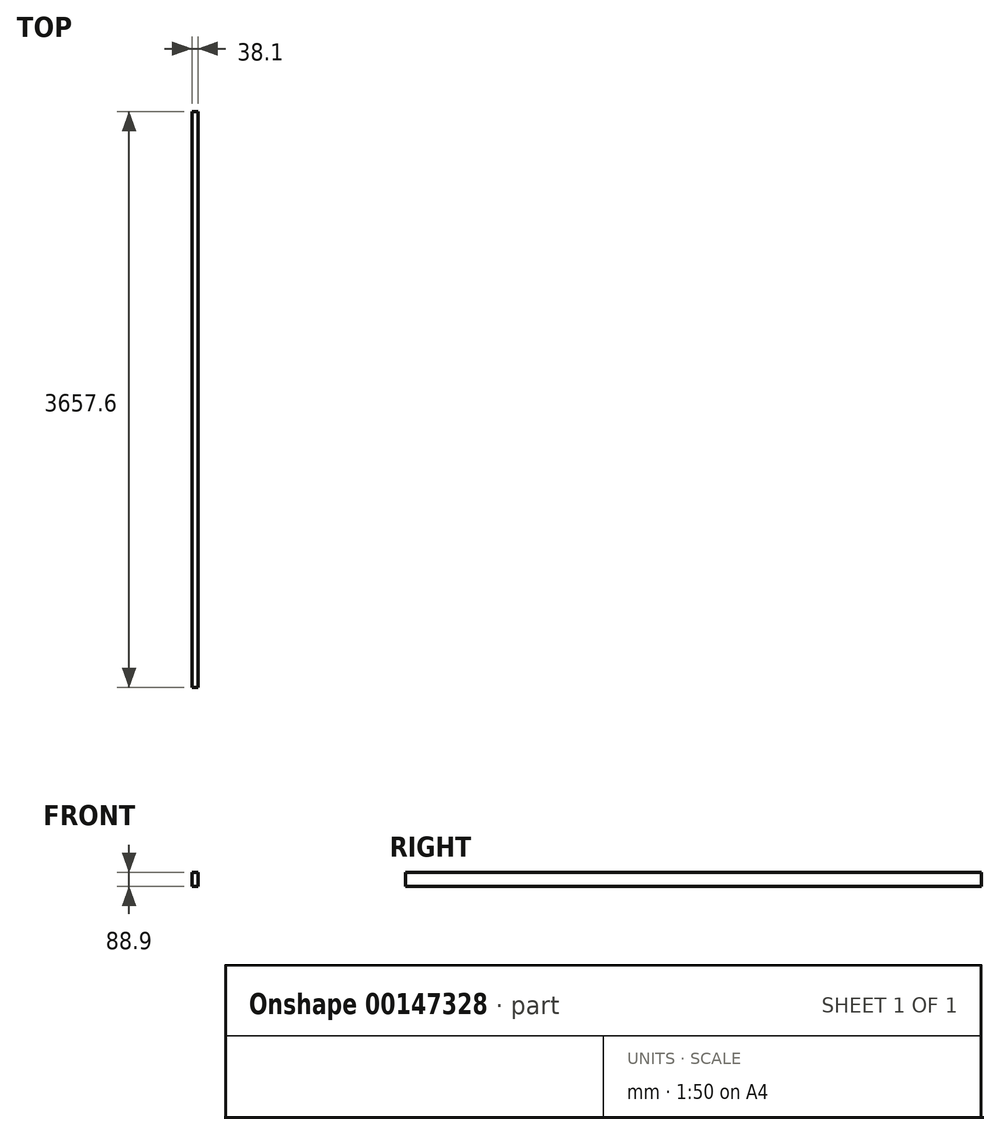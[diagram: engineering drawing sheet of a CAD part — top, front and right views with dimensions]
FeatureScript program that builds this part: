
annotation { "Feature Type Name" : "Feature", "Feature Type Description" : "" }
export const myFeature = defineFeature(function(context is Context, id is Id, definition is map)
    precondition{}
    {
        {
            var Q0;
            Q0=qCreatedBy(makeId("Front.planeOp"),FACE);
            var sketch = newSketch(context, id + "F0", { "sketchPlane" : qUnion([Q0])});
            skLineSegment(sketch, "E0.bottom", {"start": v(-18, 55.77) * mm, "end": v(20.1, 55.77) * mm});
            skLineSegment(sketch, "E0.top", {"start": v(-18, -33.13) * mm, "end": v(20.1, -33.13) * mm});
            skLineSegment(sketch, "E0.left", {"start": v(-18, 55.77) * mm, "end": v(-18, -33.13) * mm});
            skLineSegment(sketch, "E0.right", {"start": v(20.1, 55.77) * mm, "end": v(20.1, -33.13) * mm});
            skSolve(sketch);
        }
        {
            var Q0;
            Q0=qSketchRegion(id+"F0",true);
            extrude(context, id + "F1", {"entities" : qUnion([Q0]), "endBound" : BoundingType.SYMMETRIC, "depth" : 3657.6 * mm});
        }
    });
